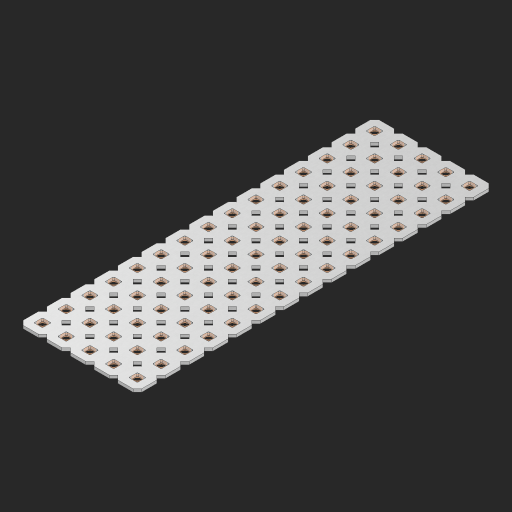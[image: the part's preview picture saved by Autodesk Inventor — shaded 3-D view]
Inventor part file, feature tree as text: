
AUTODESK INVENTOR PART (.ipt)
format: ipt  version: 2023 (Build 270158000, 158)  size: 1,158,656 bytes
history: native  units: in
note: dims shown in document units (in); Inventor stores cm internally (conversion verified against a paired STEP export)
features: other x76, extrude x74, sketch x2, pattern_linear x1
ambient origin geometry x8: Origin, YZ Plane, XZ Plane, XY Plane, X Axis, Y Axis, Z Axis, Center Point
bodies: Solid1 (feature_tree), Body (feature_tree)
feature tree (153):
  pattern_linear  "Rectangular Pattern1"  Spacing1=0.09in  [1 undecoded]
  sketch  "Sketch1"  dims[d1=0.5in]
  sketch  "Sketch2"  dims[d2=0.182in d3=0.09in d4=0.09in d5=0.09in d6=0.09in d7=0.09in d8=0.09in d9=0.09in d10=0.09in d11=0.02in d13=0.0in d14=0.172in d15=0.0625in d16=0.0in d19=0.5in d22=0.5in]
  other  "Srf1"
  other  "Srf126"
  other  "Srf127"
  other  "Srf128"
  other  "Srf129"
  other  "Srf130"
  other  "Srf131"
  other  "Srf250"
  other  "Srf251"
  other  "Srf252"
  other  "Srf253"
  other  "Srf254"
  other  "Srf255"
  other  "Srf256"
  other  "Srf257"
  other  "Srf268"
  other  "Srf269"
  other  "Srf270"
  other  "Srf271"
  other  "Srf272"
  other  "Srf273"
  other  "Srf274"
  other  "Srf275"
  other  "Srf276"
  other  "Srf277"
  other  "Srf278"
  other  "Srf279"
  other  "Srf280"
  other  "Srf281"
  other  "Srf282"
  other  "Srf293"
  other  "Srf294"
  other  "Srf295"
  other  "Srf296"
  other  "Srf297"
  other  "Srf298"
  other  "Srf299"
  other  "Srf300"
  other  "Srf301"
  other  "Srf302"
  other  "Srf303"
  other  "Srf304"
  other  "Srf305"
  other  "Srf306"
  other  "Srf307"
  other  "Srf318"
  other  "Srf319"
  other  "Srf320"
  other  "Srf321"
  other  "Srf322"
  other  "Srf323"
  other  "Srf324"
  other  "Srf325"
  other  "Srf326"
  other  "Srf327"
  other  "Srf328"
  other  "Srf329"
  other  "Srf330"
  other  "Srf331"
  other  "Srf332"
  other  "Srf343"
  other  "Srf344"
  other  "Srf345"
  other  "Srf346"
  other  "Srf347"
  other  "Srf348"
  other  "Srf349"
  other  "Srf350"
  other  "Srf351"
  other  "Srf352"
  other  "Srf353"
  other  "Srf354"
  other  "Srf355"
  other  "Srf356"
  other  "Srf357"
  other  "Circle"
  extrude  "ExtrusionSrf126"  Depth=0.09in
  extrude  "ExtrusionSrf127"  Depth=0.09in
  extrude  "ExtrusionSrf128"  Depth=0.09in
  extrude  "ExtrusionSrf129"  Depth=0.09in
  extrude  "ExtrusionSrf130"  Depth=0.09in
  extrude  "ExtrusionSrf131"  Depth=0.09in
  extrude  "ExtrusionSrf250"  Depth=0.09in
  extrude  "ExtrusionSrf251"  Depth=0.02in
  extrude  "ExtrusionSrf252"  TaperAngle=0.0deg  [1 undecoded]
  extrude  "ExtrusionSrf253"  Depth=0.5in
  extrude  "ExtrusionSrf254"  Depth=0.0625in TaperAngle=0.0deg
  extrude  "ExtrusionSrf255"  Depth=0.5in
  extrude  "ExtrusionSrf256"  Depth=0.5in
  extrude  "ExtrusionSrf257"  [1 undecoded]
  extrude  "ExtrusionSrf268"  [1 undecoded]
  extrude  "ExtrusionSrf269"  [1 undecoded]
  extrude  "ExtrusionSrf270"  [1 undecoded]
  extrude  "ExtrusionSrf271"  [1 undecoded]
  extrude  "ExtrusionSrf272"  [1 undecoded]
  extrude  "ExtrusionSrf273"  [1 undecoded]
  extrude  "ExtrusionSrf274"  [1 undecoded]
  extrude  "ExtrusionSrf275"  [1 undecoded]
  extrude  "ExtrusionSrf276"  [1 undecoded]
  extrude  "ExtrusionSrf277"  [1 undecoded]
  extrude  "ExtrusionSrf278"  [1 undecoded]
  extrude  "ExtrusionSrf279"  [1 undecoded]
  extrude  "ExtrusionSrf280"  [1 undecoded]
  extrude  "ExtrusionSrf281"  [1 undecoded]
  extrude  "ExtrusionSrf282"  [1 undecoded]
  extrude  "ExtrusionSrf293"  [1 undecoded]
  extrude  "ExtrusionSrf294"  [1 undecoded]
  extrude  "ExtrusionSrf295"  [1 undecoded]
  extrude  "ExtrusionSrf296"  [1 undecoded]
  extrude  "ExtrusionSrf297"  [1 undecoded]
  extrude  "ExtrusionSrf298"  [1 undecoded]
  extrude  "ExtrusionSrf299"  [1 undecoded]
  extrude  "ExtrusionSrf300"  [1 undecoded]
  extrude  "ExtrusionSrf301"  [1 undecoded]
  extrude  "ExtrusionSrf302"  [1 undecoded]
  extrude  "ExtrusionSrf303"  [1 undecoded]
  extrude  "ExtrusionSrf304"  [1 undecoded]
  extrude  "ExtrusionSrf305"  [1 undecoded]
  extrude  "ExtrusionSrf306"  [1 undecoded]
  extrude  "ExtrusionSrf307"  [1 undecoded]
  extrude  "ExtrusionSrf318"  [1 undecoded]
  extrude  "ExtrusionSrf319"  [1 undecoded]
  extrude  "ExtrusionSrf320"  [1 undecoded]
  extrude  "ExtrusionSrf321"  [1 undecoded]
  extrude  "ExtrusionSrf322"  [1 undecoded]
  extrude  "ExtrusionSrf323"  [1 undecoded]
  extrude  "ExtrusionSrf324"  [1 undecoded]
  extrude  "ExtrusionSrf325"  [1 undecoded]
  extrude  "ExtrusionSrf326"  [1 undecoded]
  extrude  "ExtrusionSrf327"  [1 undecoded]
  extrude  "ExtrusionSrf328"  [1 undecoded]
  extrude  "ExtrusionSrf329"  [1 undecoded]
  extrude  "ExtrusionSrf330"  [1 undecoded]
  extrude  "ExtrusionSrf331"  [1 undecoded]
  extrude  "ExtrusionSrf332"  [1 undecoded]
  extrude  "ExtrusionSrf343"  [1 undecoded]
  extrude  "ExtrusionSrf344"  [1 undecoded]
  extrude  "ExtrusionSrf345"  [1 undecoded]
  extrude  "ExtrusionSrf346"  [1 undecoded]
  extrude  "ExtrusionSrf347"  [1 undecoded]
  extrude  "ExtrusionSrf348"  [1 undecoded]
  extrude  "ExtrusionSrf349"  [1 undecoded]
  extrude  "ExtrusionSrf350"  [1 undecoded]
  extrude  "ExtrusionSrf351"  [1 undecoded]
  extrude  "ExtrusionSrf352"  [1 undecoded]
  extrude  "ExtrusionSrf353"  [1 undecoded]
  extrude  "ExtrusionSrf354"  [1 undecoded]
  extrude  "ExtrusionSrf355"  [1 undecoded]
  extrude  "ExtrusionSrf356"  [1 undecoded]
  extrude  "ExtrusionSrf357"  [1 undecoded]
note: 63 required parameter values undecoded (feature->parameter linkage not recoverable at this tier; creation-order binding heuristic only, values carry confidence <= 0.55)
